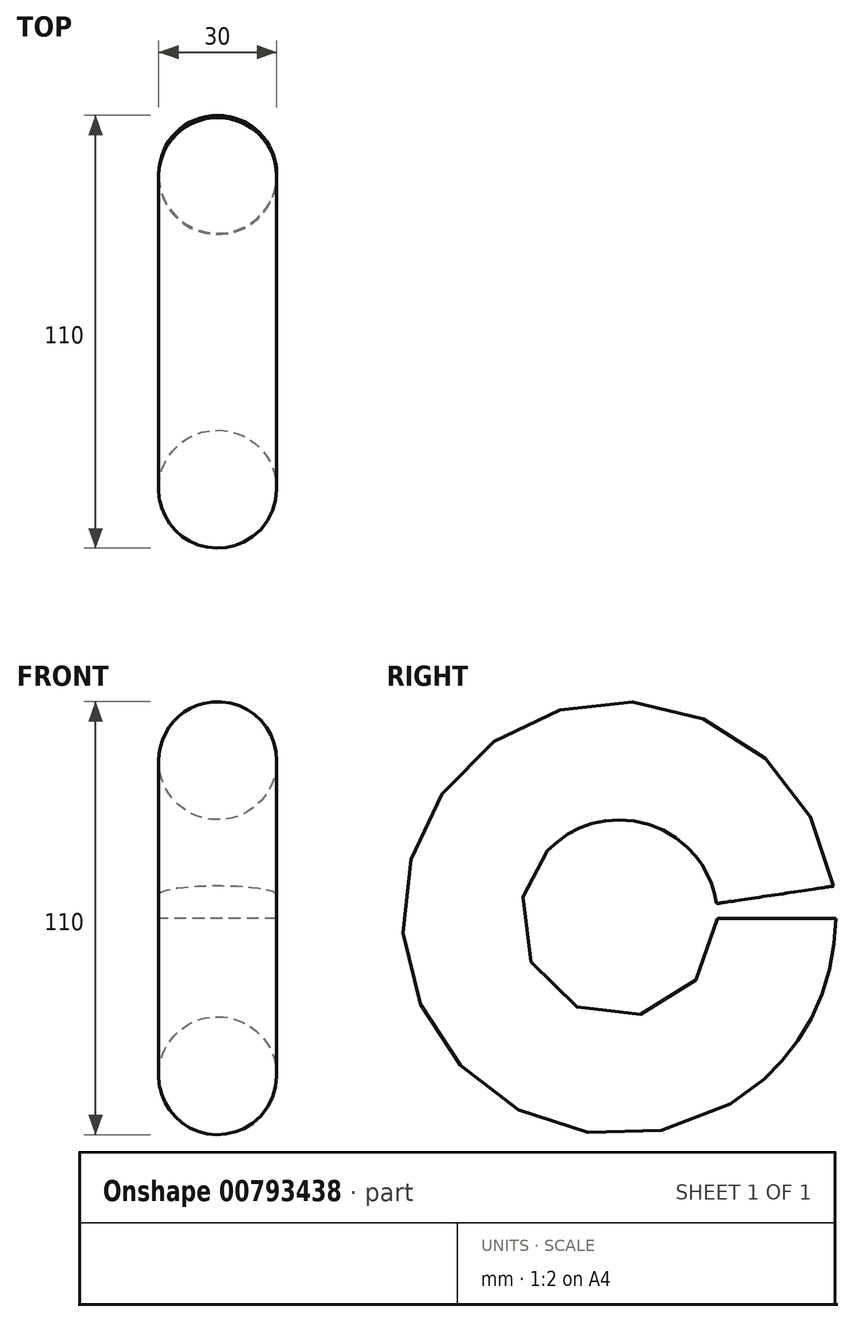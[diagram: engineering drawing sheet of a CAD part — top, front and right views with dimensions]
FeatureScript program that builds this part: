
annotation { "Feature Type Name" : "Feature", "Feature Type Description" : "" }
export const myFeature = defineFeature(function(context is Context, id is Id, definition is map)
    precondition{}
    {
        {
            var Q0;
            Q0=qCreatedBy(makeId("Right.planeOp"),FACE);
            var sketch = newSketch(context, id + "F0", { "sketchPlane" : qUnion([Q0])});
            skArc(sketch, "E0", {"start": v(39.56, 5.92) * mm, "mid": v(-39.89, -2.97) * mm, "end": v(40, 0) * mm});
            skSolve(sketch);
        }
        {
            var Q0;
            Q0=qCreatedBy(makeId("Top.planeOp"),FACE);
            var sketch = newSketch(context, id + "F1", { "sketchPlane" : qUnion([Q0])});
            skCircle(sketch, "E1", {"center": v(0, 40) * mm, "radius": 15 * mm});
            skSolve(sketch);
        }
        {
            var Q0;
            Q0=makeQuery(id+"F1.imprint","IMPRINT",FACE,{"disambiguationData":[TD([[makeQuery(id+"F1.imprint","IMPRINT",EDGE,{"derivedFrom":sQuery(id+"F1.wireOp",EDGE,"E1")}),1.0]])]});
            var Q1;
            Q1=sQuery(id+"F0.wireOp",EDGE,"E0");
            sweep(context, id + "F2", {"profiles" : qUnion([Q0]), "path" : qUnion([Q1])});
        }
    });
